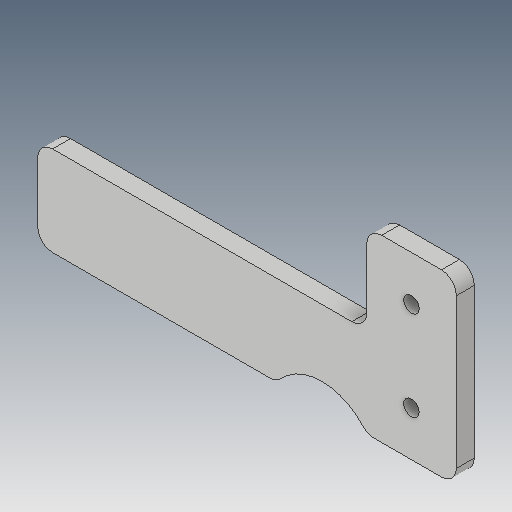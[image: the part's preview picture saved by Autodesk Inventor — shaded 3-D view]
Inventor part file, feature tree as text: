
AUTODESK INVENTOR PART (.ipt)
format: ipt  version: 2017 (Build 210142000, 142)  size: 117,248 bytes
history: native  units: mm
features: other x3, sketch x1
ambient origin geometry x8: Origin, YZ Plane, XZ Plane, XY Plane, X Axis, Y Axis, Z Axis, Center Point
bodies: Solid1 (feature_tree)
feature tree (4):
  other  "Spool Holder.ipt"
  other  "Solid1::Spool Holder.ipt"
  other  "TaggingFeature1"
  sketch  "Sketch1"  dims[d0=10.0mm]
